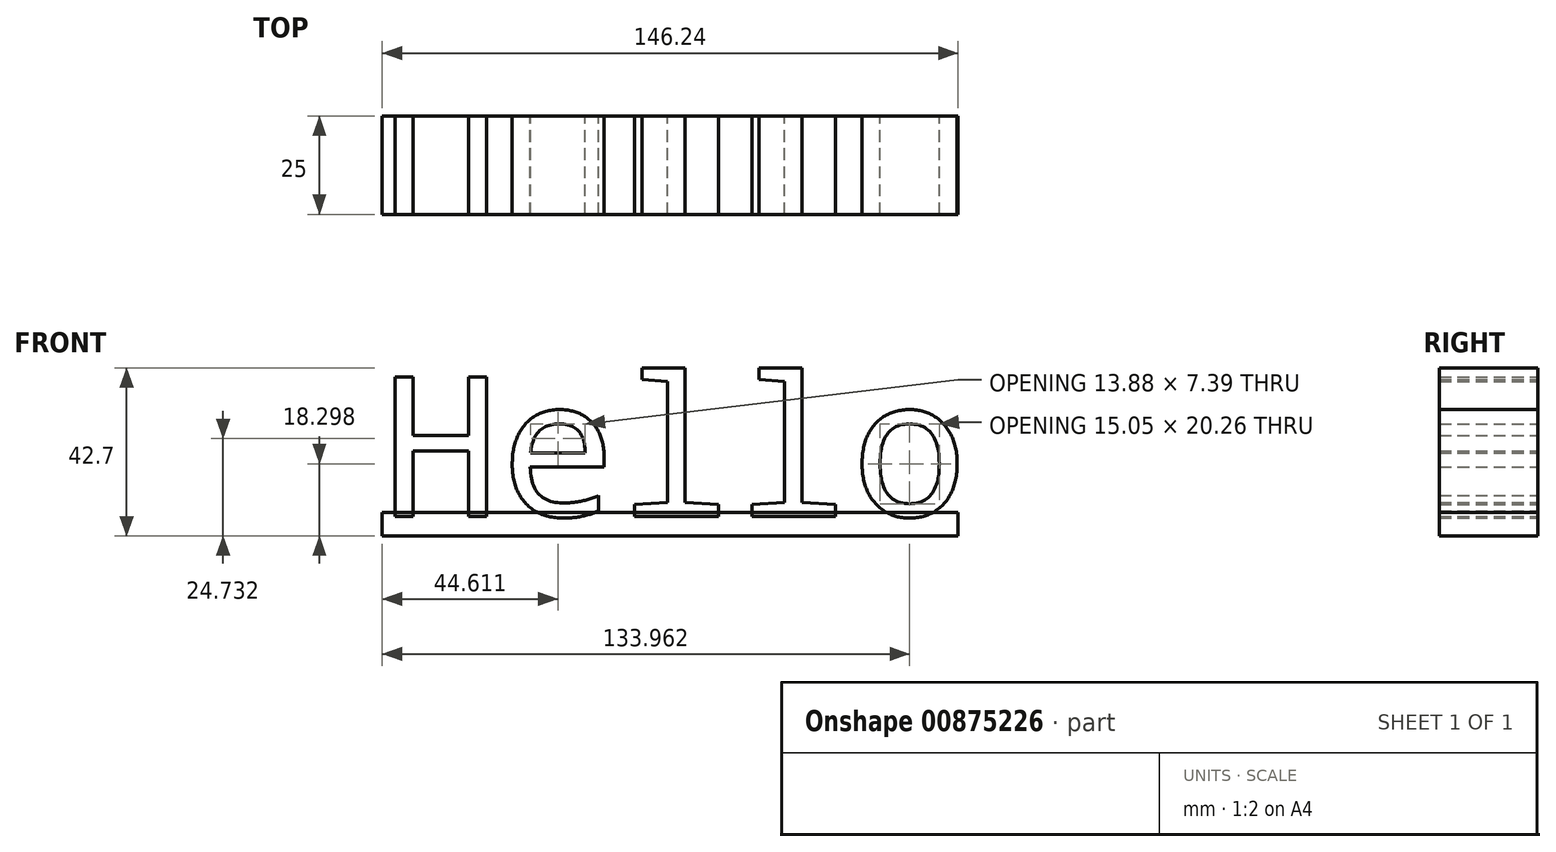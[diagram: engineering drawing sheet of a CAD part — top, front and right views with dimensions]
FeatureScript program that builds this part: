
annotation { "Feature Type Name" : "Feature", "Feature Type Description" : "" }
export const myFeature = defineFeature(function(context is Context, id is Id, definition is map)
    precondition{}
    {
        {
            var Q0;
            Q0=qCreatedBy(makeId("Front.planeOp"),FACE);
            var sketch = newSketch(context, id + "F0", { "sketchPlane" : qUnion([Q0])});
            skText(sketch, "E0", { "text": "Hello", "fontName": "DroidSansMono.ttf"});
            const initialGuessF0  = {"E0": [0, 0, 1, 0, 0.03572]};
            skSetInitialGuess(sketch, initialGuessF0);
            skSolve(sketch);
        }
        {
            var Q0;
            Q0 = qSketchRegion(id + "F0", true);
            extrude(context, id + "F1", {"entities" : qUnion([Q0]), "depth" : 25 * mm, "offsetDistance" : 25 * mm});
        }
        {
            var Q0;
            Q0=makeQuery(id+"F1.opExtrude","SWEPT_FACE",FACE,{"disambiguationData":[OSD([sQuery(id+"F0.wireOp",EDGE,"E0.sketch_text.stroke-43")])]});
            var sketch = newSketch(context, id + "F2", { "sketchPlane" : qUnion([Q0])});
            skLineSegment(sketch, "E1.bottom", {"start": v(146.24, 25) * mm, "end": v(0, 25) * mm});
            skLineSegment(sketch, "E1.top", {"start": v(146.24, 0) * mm, "end": v(0, 0) * mm});
            skLineSegment(sketch, "E1.left", {"start": v(146.24, 25) * mm, "end": v(146.24, 0) * mm});
            skLineSegment(sketch, "E1.right", {"start": v(0, 25) * mm, "end": v(0, 0) * mm});
            skSolve(sketch);
        }
        {
            var Q0;
            Q0 = qSketchRegion(id + "F2", true);
            extrude(context, id + "F3", {"entities" : qUnion([Q0]), "depth" : 5 * mm, "offsetDistance" : 25 * mm, "hasSecondDirection" : true, "secondDirectionOppositeDirection" : true, "secondDirectionDepth" : 1 * mm});
        }
    });
